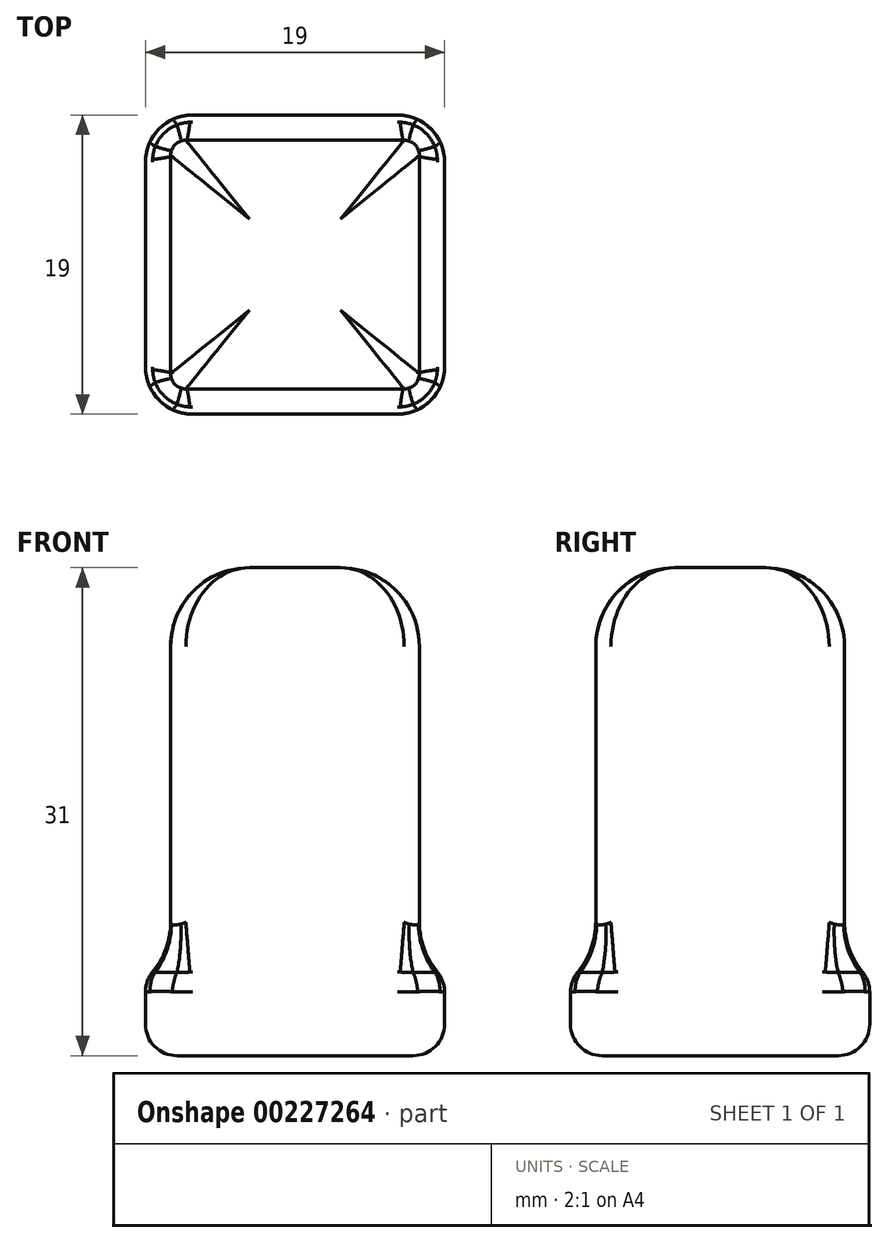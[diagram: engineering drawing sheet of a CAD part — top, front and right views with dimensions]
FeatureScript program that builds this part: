
annotation { "Feature Type Name" : "Feature", "Feature Type Description" : "" }
export const myFeature = defineFeature(function(context is Context, id is Id, definition is map)
    precondition{}
    {
        {
            var Q0;
            Q0=qCreatedBy(makeId("Top.planeOp"),FACE);
            var sketch = newSketch(context, id + "F0", { "sketchPlane" : qUnion([Q0])});
            skLineSegment(sketch, "E0.bottom", {"start": v(0, 0) * mm, "end": v(19, 0) * mm});
            skLineSegment(sketch, "E0.top", {"start": v(0, -19) * mm, "end": v(19, -19) * mm});
            skLineSegment(sketch, "E0.left", {"start": v(0, 0) * mm, "end": v(0, -19) * mm});
            skLineSegment(sketch, "E0.right", {"start": v(19, 0) * mm, "end": v(19, -19) * mm});
            skSolve(sketch);
        }
        {
            var Q0;
            Q0 = qSketchRegion(id + "F0", true);
            extrude(context, id + "F1", {"entities" : qUnion([Q0]), "depth" : 6 * mm});
        }
        {
            var Q0;
            Q0=makeQuery(id+"F1.opExtrude","CAP_FACE",FACE,{"disambiguationData":[OSD([sQuery(id+"F0.wireOp",EDGE,"E0.bottom"),sQuery(id+"F0.wireOp",EDGE,"E0.top"),sQuery(id+"F0.wireOp",EDGE,"E0.left"),sQuery(id+"F0.wireOp",EDGE,"E0.right")])],"isStart":false});
            var sketch = newSketch(context, id + "F2", { "sketchPlane" : qUnion([Q0])});
            skLineSegment(sketch, "E1.bottom", {"start": v(1.6, -1.6) * mm, "end": v(17.4, -1.6) * mm});
            skLineSegment(sketch, "E1.top", {"start": v(1.6, -17.4) * mm, "end": v(17.4, -17.4) * mm});
            skLineSegment(sketch, "E1.left", {"start": v(1.6, -1.6) * mm, "end": v(1.6, -17.4) * mm});
            skLineSegment(sketch, "E1.right", {"start": v(17.4, -1.6) * mm, "end": v(17.4, -17.4) * mm});
            skSolve(sketch);
        }
        {
            var Q0;
            Q0 = qSketchRegion(id + "F2", true);
            extrude(context, id + "F3", {"entities" : qUnion([Q0]), "operationType" : NewBodyOperationType.ADD, "depth" : 25 * mm});
        }
        {
            var Q0;
            Q0=makeQuery(id+"F3.opExtrude","SWEPT_EDGE",EDGE,{"disambiguationData":[OSD([sQuery(id+"F2.wireOp",EDGE,"E1.top"),sQuery(id+"F2.wireOp",EDGE,"E1.right")])]});
            fillet(context, id + "F4", {"entities" : qUnion([Q0]), "radius" : 0.97 * mm, "tangentPropagation" : true, "allowEdgeOverflow" : false});
        }
        {
            var Q0;
            Q0=makeQuery(id+"F3.opExtrude","SWEPT_EDGE",EDGE,{"disambiguationData":[OSD([sQuery(id+"F2.wireOp",EDGE,"E1.bottom"),sQuery(id+"F2.wireOp",EDGE,"E1.left")])]});
            fillet(context, id + "F5", {"entities" : qUnion([Q0]), "radius" : 0.97 * mm, "tangentPropagation" : true, "allowEdgeOverflow" : false});
        }
        {
            var Q0;
            Q0=makeQuery(id+"F3.opExtrude","SWEPT_EDGE",EDGE,{"disambiguationData":[OSD([sQuery(id+"F2.wireOp",EDGE,"E1.bottom"),sQuery(id+"F2.wireOp",EDGE,"E1.right")])]});
            fillet(context, id + "F6", {"entities" : qUnion([Q0]), "radius" : 0.97 * mm, "tangentPropagation" : true, "allowEdgeOverflow" : false});
        }
        {
            var Q0;
            Q0=makeQuery(id+"F3.opExtrude","SWEPT_EDGE",EDGE,{"disambiguationData":[OSD([sQuery(id+"F2.wireOp",EDGE,"E1.top"),sQuery(id+"F2.wireOp",EDGE,"E1.left")])]});
            fillet(context, id + "F7", {"entities" : qUnion([Q0]), "radius" : 0.97 * mm, "tangentPropagation" : true, "allowEdgeOverflow" : false});
        }
        {
            var Q0;
            Q0=makeQuery(id+"F1.opExtrude","SWEPT_EDGE",EDGE,{"disambiguationData":[OSD([sQuery(id+"F0.wireOp",EDGE,"E0.top"),sQuery(id+"F0.wireOp",EDGE,"E0.right")])]});
            fillet(context, id + "F8", {"entities" : qUnion([Q0]), "radius" : 3 * mm, "tangentPropagation" : true, "allowEdgeOverflow" : false});
        }
        {
            var Q0;
            Q0=makeQuery(id+"F1.opExtrude","SWEPT_EDGE",EDGE,{"disambiguationData":[OSD([sQuery(id+"F0.wireOp",EDGE,"E0.top"),sQuery(id+"F0.wireOp",EDGE,"E0.left")])]});
            fillet(context, id + "F9", {"entities" : qUnion([Q0]), "radius" : 3 * mm, "tangentPropagation" : true, "allowEdgeOverflow" : false});
        }
        {
            var Q0;
            Q0=makeQuery(id+"F1.opExtrude","SWEPT_EDGE",EDGE,{"disambiguationData":[OSD([sQuery(id+"F0.wireOp",EDGE,"E0.bottom"),sQuery(id+"F0.wireOp",EDGE,"E0.right")])]});
            fillet(context, id + "F10", {"entities" : qUnion([Q0]), "radius" : 3 * mm, "tangentPropagation" : true, "allowEdgeOverflow" : false});
        }
        {
            var Q0;
            Q0=makeQuery(id+"F1.opExtrude","SWEPT_EDGE",EDGE,{"disambiguationData":[OSD([sQuery(id+"F0.wireOp",EDGE,"E0.bottom"),sQuery(id+"F0.wireOp",EDGE,"E0.left")])]});
            fillet(context, id + "F11", {"entities" : qUnion([Q0]), "radius" : 3 * mm, "tangentPropagation" : true, "allowEdgeOverflow" : false});
        }
        {
            var Q0;
            Q0=makeQuery(id+"F3.opExtrude","CAP_EDGE",EDGE,{"disambiguationData":[OSD([sQuery(id+"F2.wireOp",EDGE,"E1.right")])],"isStart":false});
            fillet(context, id + "F12", {"entities" : qUnion([Q0]), "radius" : 5 * mm, "tangentPropagation" : true, "allowEdgeOverflow" : false});
        }
        {
            var Q0;
            Q0=makeQuery(id+"F1.opExtrude","SWEPT_FACE",FACE,{"disambiguationData":[OSD([sQuery(id+"F0.wireOp",EDGE,"E0.right")])]});
            fillet(context, id + "F13", {"entities" : qUnion([Q0]), "radius" : 2 * mm, "tangentPropagation" : true, "allowEdgeOverflow" : false});
        }
        {
            var Q0;
            {var subQ0=sQuery(id+"F0.wireOp",EDGE,"E0.top");Q0=makeQuery(id+"F13.opFillet","BLEND_FACE",FACE,{"disambiguationData":[OSD([subQ0]),TDD([makeQuery(id+"F1.opExtrude","CAP_EDGE",EDGE,{"disambiguationData":[OSD([subQ0])],"isStart":false})]),OD(0.0)]});}
            fillet(context, id + "F14", {"entities" : qUnion([Q0]), "radius" : 5 * mm, "tangentPropagation" : true, "allowEdgeOverflow" : false});
        }
    });
